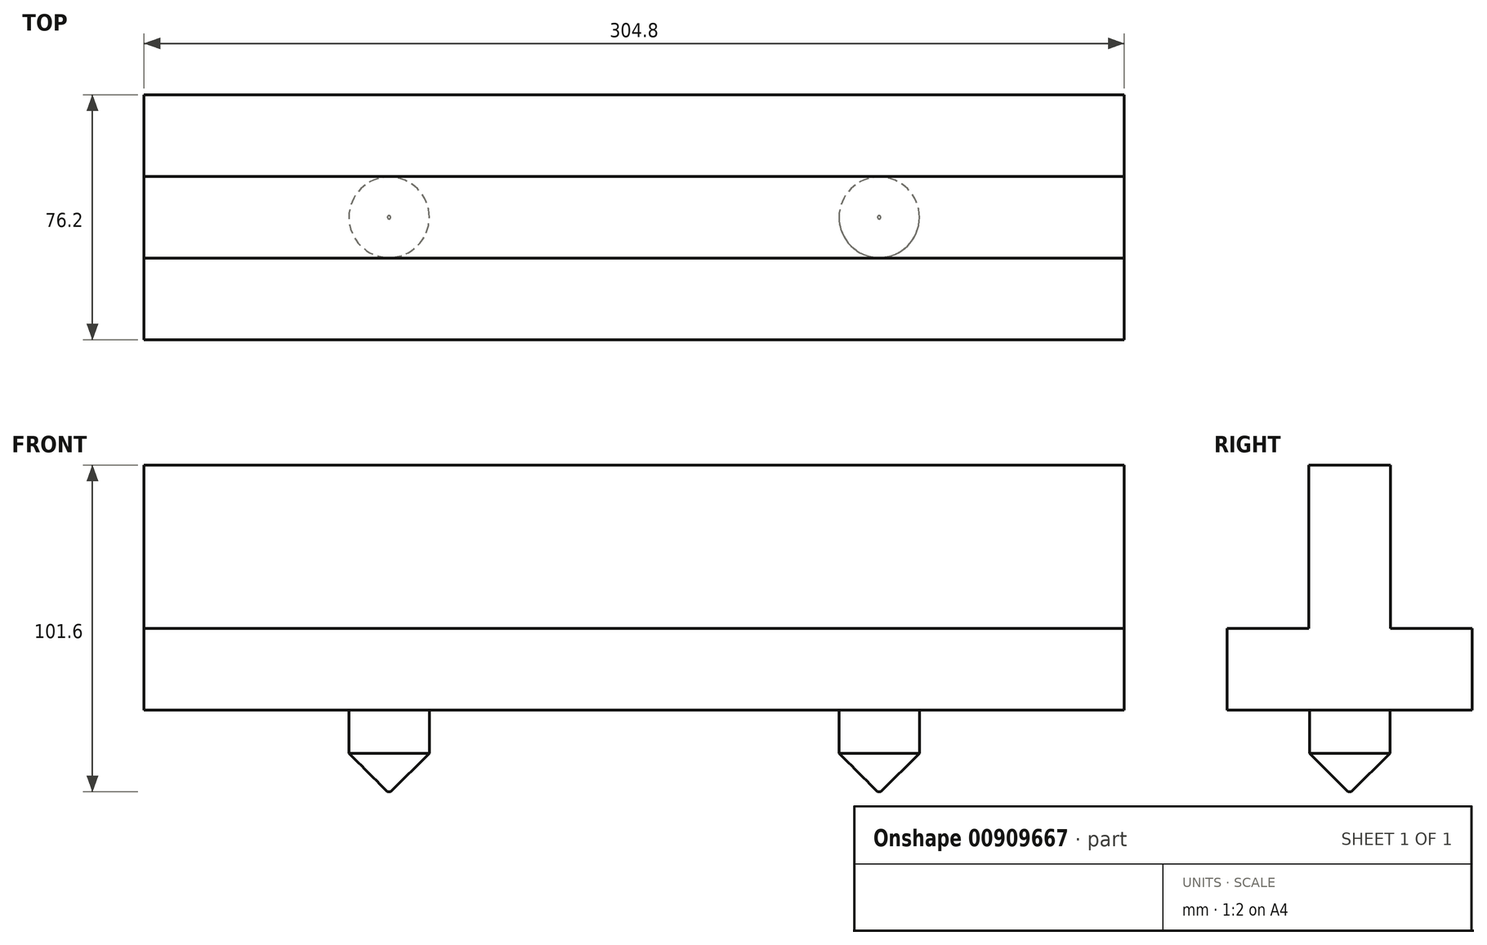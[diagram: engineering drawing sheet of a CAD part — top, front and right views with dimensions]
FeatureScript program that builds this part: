
annotation { "Feature Type Name" : "Feature", "Feature Type Description" : "" }
export const myFeature = defineFeature(function(context is Context, id is Id, definition is map)
    precondition{}
    {
        {
            var Q0;
            Q0=qCreatedBy(makeId("Top.planeOp"),FACE);
            var sketch = newSketch(context, id + "F0", { "sketchPlane" : qUnion([Q0])});
            skLineSegment(sketch, "E0.bottom", {"start": v(152.4, 38.1) * mm, "end": v(-152.4, 38.1) * mm});
            skLineSegment(sketch, "E0.top", {"start": v(152.4, -38.1) * mm, "end": v(-152.4, -38.1) * mm});
            skLineSegment(sketch, "E0.left", {"start": v(152.4, 38.1) * mm, "end": v(152.4, -38.1) * mm});
            skLineSegment(sketch, "E0.right", {"start": v(-152.4, 38.1) * mm, "end": v(-152.4, -38.1) * mm});
            skPoint(sketch, "E0.middle", {"position": v(0, 0) * mm});
            skSolve(sketch);
        }
        {
            var Q0;
            Q0 = qSketchRegion(id + "F0", true);
            extrude(context, id + "F1", {"entities" : qUnion([Q0]), "depth" : 25.4 * mm, "offsetDistance" : 25 * mm});
        }
        {
            var Q0;
            Q0=makeQuery(id+"F1.opExtrude","CAP_FACE",FACE,{"disambiguationData":[OSD([sQuery(id+"F0.wireOp",EDGE,"E0.bottom"),sQuery(id+"F0.wireOp",EDGE,"E0.top"),sQuery(id+"F0.wireOp",EDGE,"E0.left"),sQuery(id+"F0.wireOp",EDGE,"E0.right")])],"isStart":false});
            var sketch = newSketch(context, id + "F2", { "sketchPlane" : qUnion([Q0])});
            skLineSegment(sketch, "E1.bottom", {"start": v(152.4, 12.7) * mm, "end": v(-152.4, 12.7) * mm});
            skLineSegment(sketch, "E1.top", {"start": v(152.4, -12.7) * mm, "end": v(-152.4, -12.7) * mm});
            skLineSegment(sketch, "E1.left", {"start": v(152.4, 12.7) * mm, "end": v(152.4, -12.7) * mm});
            skLineSegment(sketch, "E1.right", {"start": v(-152.4, 12.7) * mm, "end": v(-152.4, -12.7) * mm});
            skPoint(sketch, "E1.middle", {"position": v(0, 0) * mm});
            skSolve(sketch);
        }
        {
            var Q0;
            Q0 = qSketchRegion(id + "F2", true);
            extrude(context, id + "F3", {"entities" : qUnion([Q0]), "operationType" : NewBodyOperationType.ADD, "depth" : 50.8 * mm, "offsetDistance" : 25 * mm});
        }
        {
            var Q0;
            Q0=makeQuery(id+"F1.opExtrude","CAP_FACE",FACE,{"disambiguationData":[OSD([sQuery(id+"F0.wireOp",EDGE,"E0.bottom"),sQuery(id+"F0.wireOp",EDGE,"E0.top"),sQuery(id+"F0.wireOp",EDGE,"E0.left"),sQuery(id+"F0.wireOp",EDGE,"E0.right")])],"isStart":true});
            var sketch = newSketch(context, id + "F4", { "sketchPlane" : qUnion([Q0])});
            skCircle(sketch, "E2", {"center": v(-76.2, 0) * mm, "radius": 12.5 * mm});
            skCircle(sketch, "E3", {"center": v(76.2, 0) * mm, "radius": 12.5 * mm});
            skSolve(sketch);
        }
        {
            var Q0;
            Q0 = qSketchRegion(id + "F4", true);
            extrude(context, id + "F5", {"entities" : qUnion([Q0]), "operationType" : NewBodyOperationType.ADD, "depth" : 25.4 * mm, "offsetDistance" : 25 * mm});
        }
        {
            var Q0;
            Q0=makeQuery(id+"F5.opExtrude","CAP_EDGE",EDGE,{"disambiguationData":[OSD([sQuery(id+"F4.wireOp",EDGE,"E2")])],"isStart":false});
            var Q1;
            Q1=makeQuery(id+"F5.opExtrude","CAP_EDGE",EDGE,{"disambiguationData":[OSD([sQuery(id+"F4.wireOp",EDGE,"E3")])],"isStart":false});
            chamfer(context, id + "F6", {"entities" : qUnion([Q0, Q1]), "width" : 12 * mm, "tangentPropagation" : true});
        }
    });
